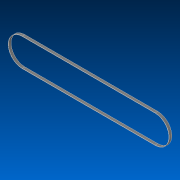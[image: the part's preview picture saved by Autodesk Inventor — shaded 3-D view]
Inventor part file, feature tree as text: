
AUTODESK INVENTOR PART (.ipt)
format: ipt  version: 2022 (Build 260153000, 153)  size: 94,720 bytes
history: native  units: in
note: dims shown in document units (in); Inventor stores cm internally (conversion verified against a paired STEP export)
features: extrude x1, sketch x1
ambient origin geometry x8: Origin, YZ Plane, XZ Plane, XY Plane, X Axis, Y Axis, Z Axis, Center Point
bodies: Solid1 (feature_tree)
feature tree (2):
  extrude  "Extrusion1"  Depth=3.76in
  sketch  "Sketch1"  dims[d0=18.0697in d1=3.76in d2=0.0394in d3=0.3543in d4=0.0in]
